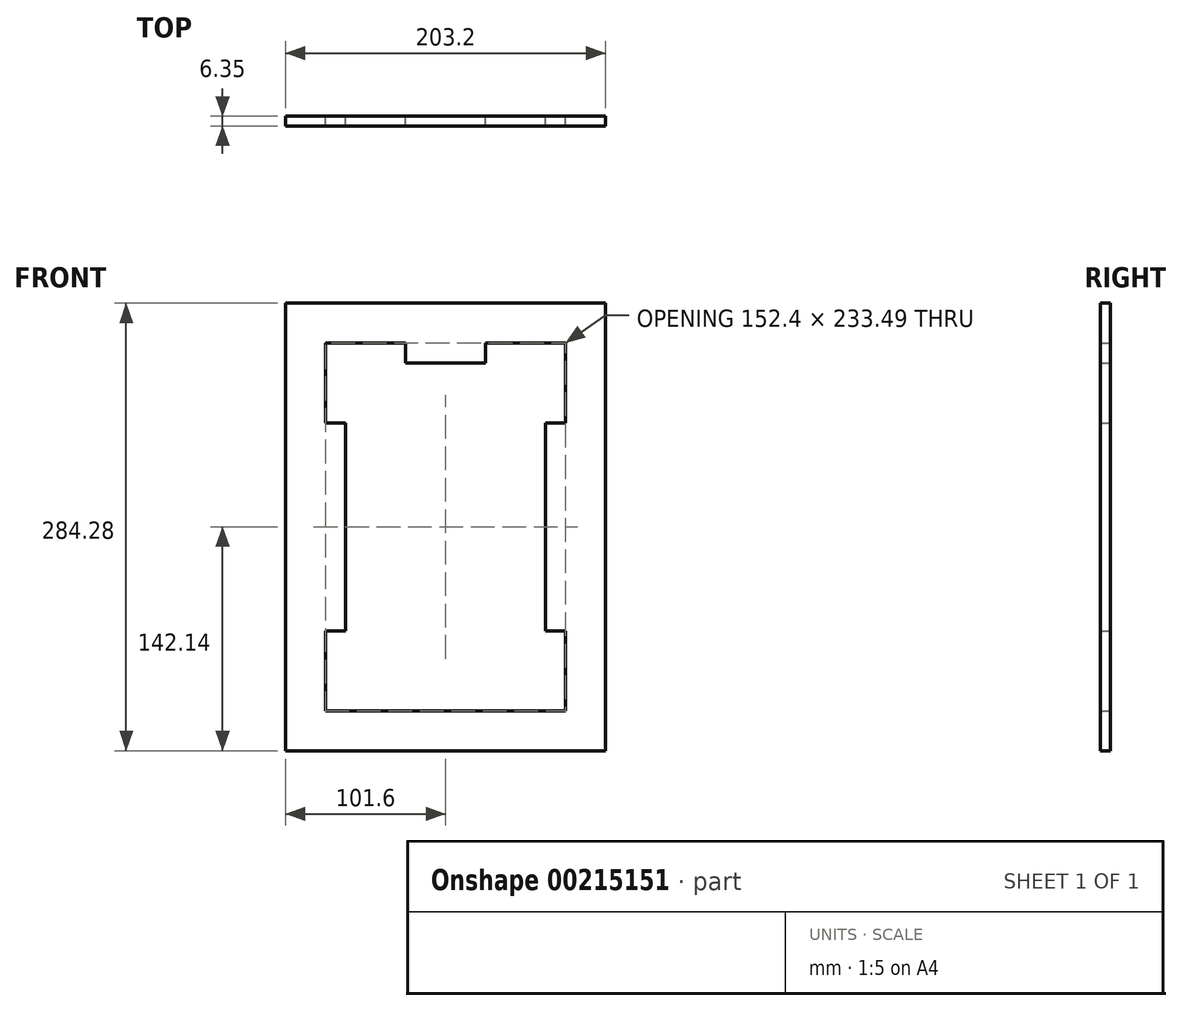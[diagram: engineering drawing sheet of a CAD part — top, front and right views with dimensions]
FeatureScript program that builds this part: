
annotation { "Feature Type Name" : "Feature", "Feature Type Description" : "" }
export const myFeature = defineFeature(function(context is Context, id is Id, definition is map)
    precondition{}
    {
        {
            var Q0;
            Q0=qCreatedBy(makeId("Front.planeOp"),FACE);
            var sketch = newSketch(context, id + "F0", { "sketchPlane" : qUnion([Q0])});
            skLineSegment(sketch, "E0.bottom", {"start": v(101.6, -129.44) * mm, "end": v(-101.6, -129.44) * mm});
            skLineSegment(sketch, "E0.top", {"start": v(101.6, 129.44) * mm, "end": v(-101.6, 129.44) * mm});
            skLineSegment(sketch, "E0.left", {"start": v(101.6, -129.44) * mm, "end": v(101.6, 129.44) * mm});
            skLineSegment(sketch, "E0.right", {"start": v(-101.6, -129.44) * mm, "end": v(-101.6, 129.44) * mm});
            skPoint(sketch, "E0.middle", {"position": v(0, 0) * mm});
            skLineSegment(sketch, "E1", {"start": v(-63.5, -129.44) * mm, "end": v(-63.5, 91.34) * mm});
            skLineSegment(sketch, "E2", {"start": v(-63.5, 91.34) * mm, "end": v(63.5, 91.34) * mm});
            skLineSegment(sketch, "E3", {"start": v(63.5, 91.34) * mm, "end": v(63.5, -129.44) * mm});
            skLineSegment(sketch, "E4", {"start": v(-63.5, 53.24) * mm, "end": v(-76.2, 53.24) * mm});
            skLineSegment(sketch, "E5", {"start": v(-76.2, 53.24) * mm, "end": v(-76.2, 104.04) * mm});
            skLineSegment(sketch, "E6", {"start": v(-76.2, 104.04) * mm, "end": v(-25.4, 104.04) * mm});
            skLineSegment(sketch, "E7", {"start": v(-25.4, 104.04) * mm, "end": v(-25.4, 91.34) * mm});
            skLineSegment(sketch, "E8", {"start": v(25.4, 91.34) * mm, "end": v(25.4, 104.04) * mm});
            skLineSegment(sketch, "E9", {"start": v(25.4, 104.04) * mm, "end": v(76.2, 104.04) * mm});
            skLineSegment(sketch, "E10", {"start": v(76.2, 104.04) * mm, "end": v(76.2, 53.24) * mm});
            skLineSegment(sketch, "E11", {"start": v(76.2, 53.24) * mm, "end": v(63.5, 53.24) * mm});
            skLineSegment(sketch, "E12.top", {"start": v(101.6, -154.84) * mm, "end": v(-101.6, -154.84) * mm});
            skLineSegment(sketch, "E12.left", {"start": v(101.6, -129.44) * mm, "end": v(101.6, -154.84) * mm});
            skLineSegment(sketch, "E12.right", {"start": v(-101.6, -129.44) * mm, "end": v(-101.6, -154.84) * mm});
            skLineSegment(sketch, "E13", {"start": v(-76.2, -129.44) * mm, "end": v(-76.2, -78.64) * mm});
            skLineSegment(sketch, "E14", {"start": v(-76.2, -78.64) * mm, "end": v(-63.5, -78.64) * mm});
            skLineSegment(sketch, "E15", {"start": v(63.5, -78.64) * mm, "end": v(76.2, -78.64) * mm});
            skLineSegment(sketch, "E16", {"start": v(76.2, -78.64) * mm, "end": v(76.2, -129.44) * mm});
            skSolve(sketch);
        }
        {
            var Q0;
            Q0=makeQuery(id+"F0.imprint","IMPRINT",FACE,{"disambiguationData":[TD([[makeQuery(id+"F0.imprint","IMPRINT",EDGE,{"derivedFrom":sQuery(id+"F0.wireOp",EDGE,"E0.top")}),1.0]])]});
            var Q1;
            Q1=makeQuery(id+"F0.imprint","IMPRINT",FACE,{"disambiguationData":[TD([[makeQuery(id+"F0.imprint","IMPRINT",EDGE,{"derivedFrom":sQuery(id+"F0.wireOp",EDGE,"E12.top")}),-1.0]])]});
            extrude(context, id + "F1", {"entities" : qUnion([Q0, Q1]), "depth" : 6.35 * mm});
        }
    });
